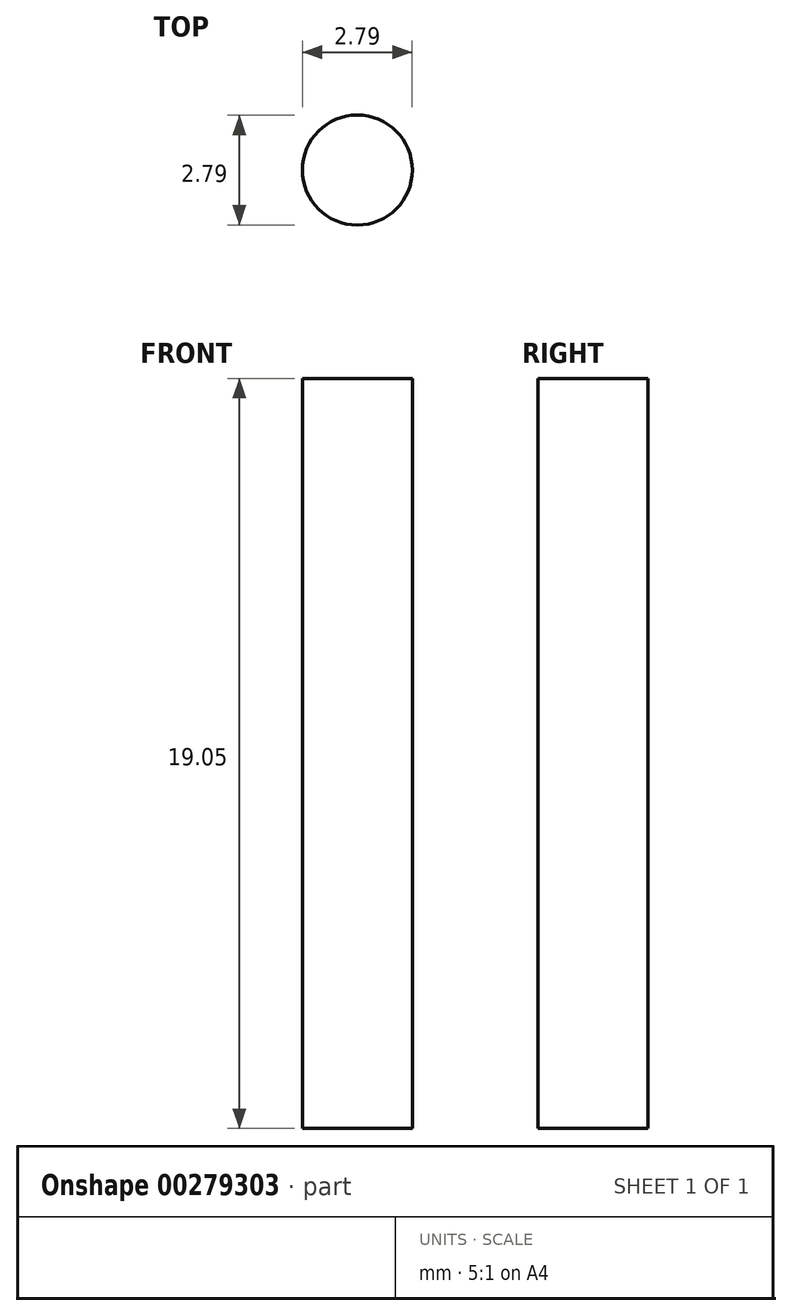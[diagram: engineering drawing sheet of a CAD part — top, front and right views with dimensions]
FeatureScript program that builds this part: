
annotation { "Feature Type Name" : "Feature", "Feature Type Description" : "" }
export const myFeature = defineFeature(function(context is Context, id is Id, definition is map)
    precondition{}
    {
        {
            var Q0;
            Q0=qCreatedBy(makeId("Top.planeOp"),FACE);
            var sketch = newSketch(context, id + "F0", { "sketchPlane" : qUnion([Q0])});
            skCircle(sketch, "E0", {"center": v(-39.76, 32.88) * mm, "radius": 1.4 * mm});
            skSolve(sketch);
        }
        {
            var Q0;
            Q0 = qSketchRegion(id + "F0", true);
            extrude(context, id + "F1", {"entities" : qUnion([Q0]), "flatOperationType" : FlatOperationType.REMOVE, "offsetDistance" : 25.4 * mm, "depth" : 19.05 * mm, "domain" : OperationDomain.MODEL});
        }
    });
